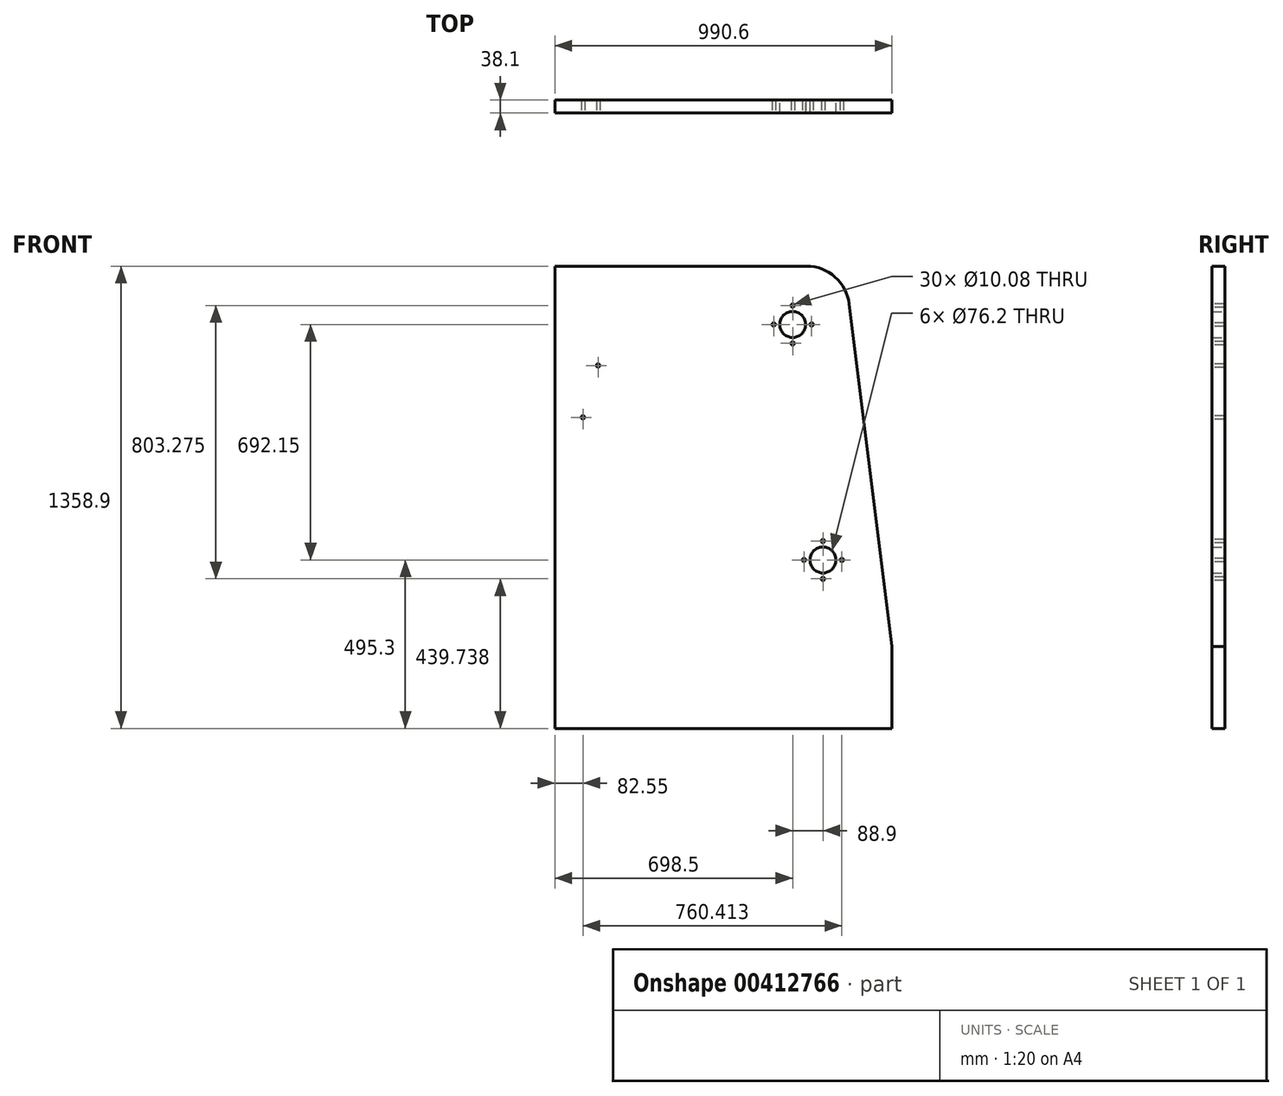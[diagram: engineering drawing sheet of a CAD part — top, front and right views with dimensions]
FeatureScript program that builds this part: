
annotation { "Feature Type Name" : "Feature", "Feature Type Description" : "" }
export const myFeature = defineFeature(function(context is Context, id is Id, definition is map)
    precondition{}
    {
        {
            var Q0;
            Q0=qCreatedBy(makeId("Front.planeOp"),FACE);
            var sketch = newSketch(context, id + "F0", { "sketchPlane" : qUnion([Q0])});
            skLineSegment(sketch, "E0", {"start": v(0, 0) * mm, "end": v(0, 1358.9) * mm});
            skLineSegment(sketch, "E1", {"start": v(990.6, 0) * mm, "end": v(0, 0) * mm});
            skLineSegment(sketch, "E2", {"start": v(990.6, 0) * mm, "end": v(990.6, 241.3) * mm});
            skLineSegment(sketch, "E3", {"start": v(990.6, 241.3) * mm, "end": v(864.8, 1247.65) * mm});
            skLineSegment(sketch, "E4", {"start": v(738.79, 1358.9) * mm, "end": v(0, 1358.9) * mm});
            skPoint(sketch, "E5.visualSharp", {"position": v(850.9, 1358.9) * mm});
            skArc(sketch, "E5.filletArc", {"start": v(864.8, 1247.65) * mm, "mid": v(822.84, 1327.1) * mm, "end": v(738.79, 1358.9) * mm});
            skCircle(sketch, "E6", {"center": v(698.5, 1187.45) * mm, "radius": 38.1 * mm});
            skCircle(sketch, "E7", {"center": v(787.4, 495.3) * mm, "radius": 38.1 * mm});
            skSolve(sketch);
        }
        {
            var Q0;
            Q0=qSketchRegion(id+"F0",true);
            extrude(context, id + "F1", {"entities" : qUnion([Q0]), "depth" : 38.1 * mm, "offsetDistance" : 25.4 * mm});
        }
        {
            var Q0;
            Q0=makeQuery(id+"F1.opExtrude","CAP_FACE",FACE,{"disambiguationData":[OSD([sQuery(id+"F0.wireOp",EDGE,"E0"),sQuery(id+"F0.wireOp",EDGE,"E1"),sQuery(id+"F0.wireOp",EDGE,"E2"),sQuery(id+"F0.wireOp",EDGE,"E3"),sQuery(id+"F0.wireOp",EDGE,"E4"),sQuery(id+"F0.wireOp",EDGE,"E5.filletArc")])],"isStart":false});
            var sketch = newSketch(context, id + "F2", { "sketchPlane" : qUnion([Q0])});
            skPoint(sketch, "E8", {"position": v(82.55, 914.4) * mm});
            skPoint(sketch, "E9", {"position": v(127, 1066.8) * mm});
            skCircle(sketch, "E10", {"center": v(698.5, 1187.45) * mm, "radius": 55.56 * mm, "construction": true});
            skLineSegment(sketch, "E11", {"start": v(698.5, 1243.01) * mm, "end": v(698.5, 1225.55) * mm, "construction": true});
            skLineSegment(sketch, "E12", {"start": v(698.5, 1149.35) * mm, "end": v(698.5, 1131.89) * mm, "construction": true});
            skLineSegment(sketch, "E13", {"start": v(660.4, 1187.45) * mm, "end": v(642.94, 1187.45) * mm, "construction": true});
            skLineSegment(sketch, "E14", {"start": v(736.6, 1187.45) * mm, "end": v(754.06, 1187.45) * mm, "construction": true});
            skPoint(sketch, "E15", {"position": v(698.5, 1243.01) * mm});
            skPoint(sketch, "E16", {"position": v(754.06, 1187.45) * mm});
            skPoint(sketch, "E17", {"position": v(698.5, 1131.89) * mm});
            skPoint(sketch, "E18", {"position": v(642.94, 1187.45) * mm});
            skCircle(sketch, "E19", {"center": v(787.4, 495.3) * mm, "radius": 55.56 * mm, "construction": true});
            skLineSegment(sketch, "E20", {"start": v(749.3, 495.3) * mm, "end": v(731.84, 495.3) * mm, "construction": true});
            skLineSegment(sketch, "E21", {"start": v(787.4, 533.4) * mm, "end": v(787.4, 550.86) * mm, "construction": true});
            skLineSegment(sketch, "E22", {"start": v(825.5, 495.3) * mm, "end": v(842.96, 495.3) * mm, "construction": true});
            skLineSegment(sketch, "E23", {"start": v(787.4, 457.2) * mm, "end": v(787.4, 439.74) * mm, "construction": true});
            skPoint(sketch, "E24", {"position": v(787.4, 550.86) * mm});
            skPoint(sketch, "E25", {"position": v(731.84, 495.3) * mm});
            skPoint(sketch, "E26", {"position": v(787.4, 439.74) * mm});
            skPoint(sketch, "E27", {"position": v(842.96, 495.3) * mm});
            skSolve(sketch);
        }
        {
            var Q0;
            Q0=sQuery(id+"F2.wireOp",VERTEX,"E8");
            var Q1;
            Q1=sQuery(id+"F2.wireOp",VERTEX,"E9");
            var Q2;
            Q2=sQuery(id+"F2.wireOp",VERTEX,"4d729e6d-f74e-49c5-99c2-7a1ce0921ae9");
            var Q3;
            Q3=sQuery(id+"F2.wireOp",VERTEX,"E15");
            var Q4;
            Q4=sQuery(id+"F2.wireOp",VERTEX,"E16");
            var Q5;
            Q5=sQuery(id+"F2.wireOp",VERTEX,"E17");
            var Q6;
            Q6=sQuery(id+"F2.wireOp",VERTEX,"E18");
            var Q7;
            Q7=sQuery(id+"F2.wireOp",VERTEX,"E27");
            var Q8;
            Q8=sQuery(id+"F2.wireOp",VERTEX,"E24");
            var Q9;
            Q9=sQuery(id+"F2.wireOp",VERTEX,"E25");
            var Q10;
            Q10=sQuery(id+"F2.wireOp",VERTEX,"E26");
            var Q11;
            Q11=makeQuery(id+"F1.opExtrude","SWEPT_BODY",BODY,{"disambiguationData":[OSD([sQuery(id+"F0.wireOp",EDGE,"E0"),sQuery(id+"F0.wireOp",EDGE,"E1"),sQuery(id+"F0.wireOp",EDGE,"E2"),sQuery(id+"F0.wireOp",EDGE,"E3"),sQuery(id+"F0.wireOp",EDGE,"E4"),sQuery(id+"F0.wireOp",EDGE,"E5.filletArc")])]});
            hole(context, id + "F3", {"style" : HoleStyle.SIMPLE, "endStyle" : HoleEndStyle.THROUGH, "standardTappedOrClearance" : lookupTablePath({ "standard" : "ANSI", "fit" : "Normal (ASME)", "size" : "3/8", "type" : "Clearance" }), "standardBlindInLast" : lookupTablePath({ "fit" : "Free", "standard" : "ANSI", "size" : "3/8", "type" : "Clearance" }), "holeDiameter" : 10.08 * mm, "tappedDepth" : 20.65 * mm, "tapClearance" : 3, "startFromSketch" : true, "locations" : qUnion([Q0, Q1, Q2, Q3, Q4, Q5, Q6, Q7, Q8, Q9, Q10]), "scope" : qUnion([Q11])});
        }
    });
